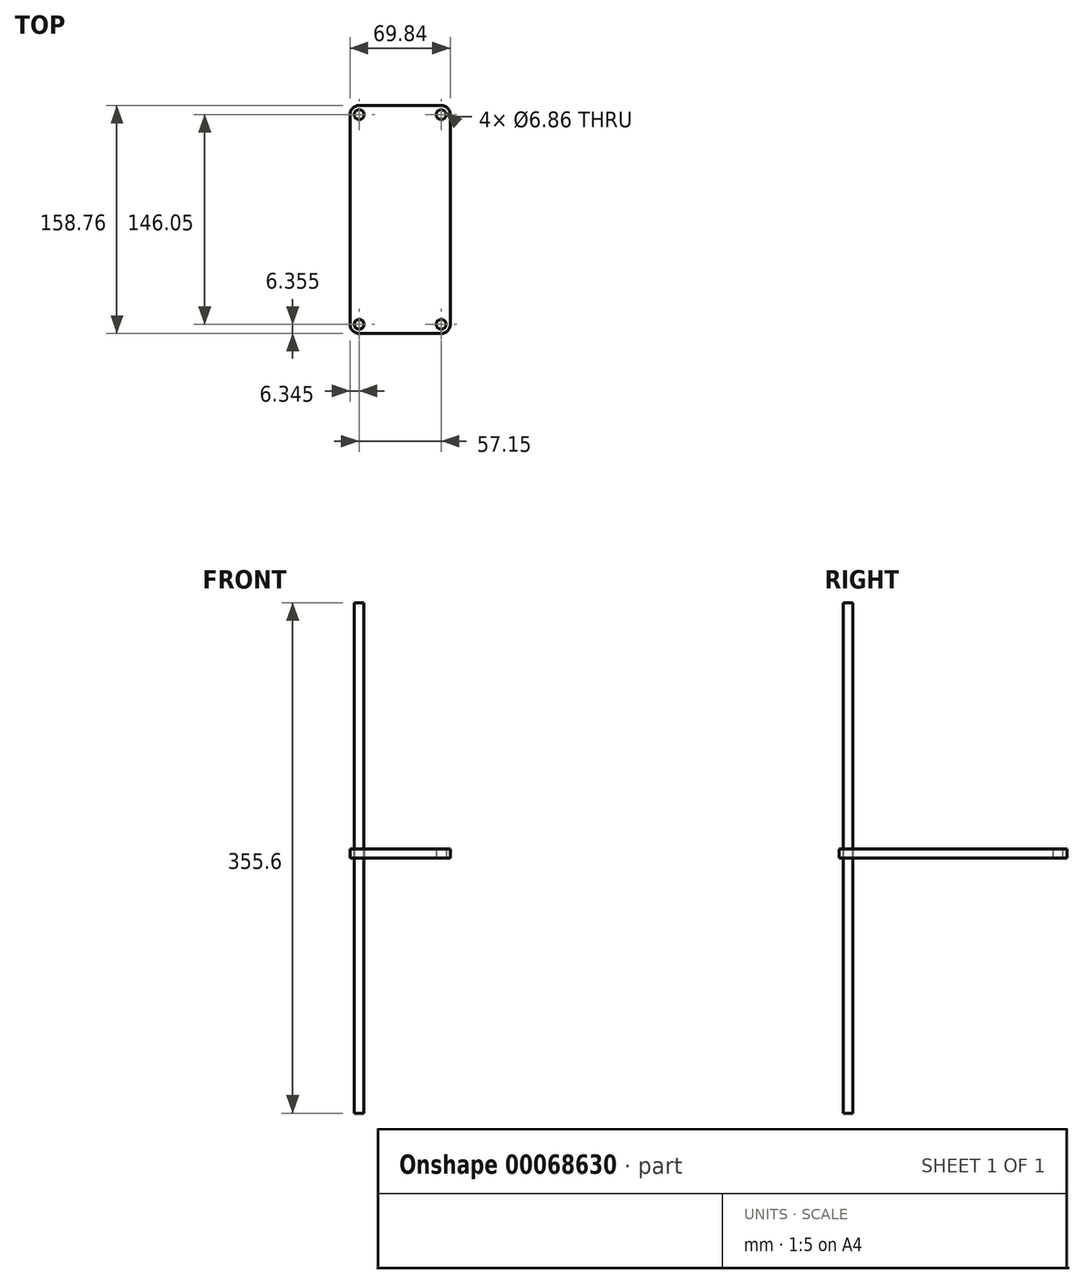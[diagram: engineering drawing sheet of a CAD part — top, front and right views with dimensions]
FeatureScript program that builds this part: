
annotation { "Feature Type Name" : "Feature", "Feature Type Description" : "" }
export const myFeature = defineFeature(function(context is Context, id is Id, definition is map)
    precondition{}
    {
        {
            var Q0;
            Q0=qCreatedBy(makeId("Top.planeOp"),FACE);
            var sketch = newSketch(context, id + "F0", { "sketchPlane" : qUnion([Q0])});
            skLineSegment(sketch, "E0", {"start": v(0, 79.38) * mm, "end": v(28.57, 79.38) * mm});
            skLineSegment(sketch, "E1", {"start": v(34.92, 73.03) * mm, "end": v(34.93, 0) * mm});
            skLineSegment(sketch, "E2.MirrorCS", {"start": v(0, 79.38) * mm, "end": v(-28.57, 79.38) * mm});
            skLineSegment(sketch, "E3.MirrorCS", {"start": v(-34.92, 73.03) * mm, "end": v(-34.93, 0) * mm});
            skLineSegment(sketch, "E4.MirrorCS", {"start": v(0, -79.38) * mm, "end": v(28.58, -79.38) * mm});
            skLineSegment(sketch, "E5.MirrorCS", {"start": v(34.93, -73.03) * mm, "end": v(34.93, 0) * mm});
            skLineSegment(sketch, "E6.MirrorCS", {"start": v(-34.93, -73.03) * mm, "end": v(-34.93, 0) * mm});
            skLineSegment(sketch, "E7.MirrorCS", {"start": v(0, -79.38) * mm, "end": v(-28.58, -79.38) * mm});
            skPoint(sketch, "E8.visualSharp", {"position": v(-34.92, 79.38) * mm});
            skArc(sketch, "E8.filletArc", {"start": v(-28.57, 79.38) * mm, "mid": v(-33.07, 77.52) * mm, "end": v(-34.93, 73.03) * mm});
            skPoint(sketch, "E9.visualSharp", {"position": v(-34.93, -79.38) * mm});
            skArc(sketch, "E9.filletArc", {"start": v(-34.93, -73.03) * mm, "mid": v(-33.07, -77.52) * mm, "end": v(-28.58, -79.37) * mm});
            skPoint(sketch, "E10.visualSharp", {"position": v(34.93, -79.38) * mm});
            skArc(sketch, "E10.filletArc", {"start": v(28.58, -79.38) * mm, "mid": v(33.07, -77.52) * mm, "end": v(34.93, -73.03) * mm});
            skPoint(sketch, "E11.visualSharp", {"position": v(34.92, 79.38) * mm});
            skArc(sketch, "E11.filletArc", {"start": v(34.92, 73.03) * mm, "mid": v(33.07, 77.52) * mm, "end": v(28.57, 79.37) * mm});
            skCircle(sketch, "E12", {"center": v(-28.57, 73.02) * mm, "radius": 3.43 * mm});
            skCircle(sketch, "E13", {"center": v(-28.58, -73.02) * mm, "radius": 3.43 * mm});
            skCircle(sketch, "E14", {"center": v(28.57, 73.02) * mm, "radius": 3.43 * mm});
            skCircle(sketch, "E15", {"center": v(28.58, -73.02) * mm, "radius": 3.43 * mm});
            skSolve(sketch);
        }
        {
            var Q0;
            Q0=makeQuery(id+"F0.imprint","IMPRINT",FACE,{"disambiguationData":[TD([[makeQuery(id+"F0.imprint","IMPRINT",EDGE,{"derivedFrom":sQuery(id+"F0.wireOp",EDGE,"E0")}),-1.0]])]});
            extrude(context, id + "F1", {"entities" : qUnion([Q0]), "depth" : 6.35 * mm});
        }
        {
            var Q0;
            Q0=makeQuery(id+"F1.opExtrude","CAP_FACE",FACE,{"disambiguationData":[OSD([sQuery(id+"F0.wireOp",EDGE,"E0"),sQuery(id+"F0.wireOp",EDGE,"E1"),sQuery(id+"F0.wireOp",EDGE,"E2.MirrorCS"),sQuery(id+"F0.wireOp",EDGE,"E3.MirrorCS"),sQuery(id+"F0.wireOp",EDGE,"E4.MirrorCS"),sQuery(id+"F0.wireOp",EDGE,"E5.MirrorCS"),sQuery(id+"F0.wireOp",EDGE,"E6.MirrorCS"),sQuery(id+"F0.wireOp",EDGE,"E7.MirrorCS"),sQuery(id+"F0.wireOp",EDGE,"E8.filletArc"),sQuery(id+"F0.wireOp",EDGE,"E9.filletArc"),sQuery(id+"F0.wireOp",EDGE,"E10.filletArc"),sQuery(id+"F0.wireOp",EDGE,"E11.filletArc"),sQuery(id+"F0.wireOp",EDGE,"E12"),sQuery(id+"F0.wireOp",EDGE,"E13"),sQuery(id+"F0.wireOp",EDGE,"E14"),sQuery(id+"F0.wireOp",EDGE,"E15")])],"isStart":true});
            var sketch = newSketch(context, id + "F2", { "sketchPlane" : qUnion([Q0])});
            skCircle(sketch, "E16", {"center": v(-28.58, 73.02) * mm, "radius": 3.28 * mm});
            skSolve(sketch);
        }
        {
            var Q0;
            Q0=makeQuery(id+"F2.imprint","IMPRINT",FACE,{"disambiguationData":[TD([[makeQuery(id+"F2.imprint","IMPRINT",EDGE,{"derivedFrom":sQuery(id+"F2.wireOp",EDGE,"E16")}),1.0]])]});
            extrude(context, id + "F3", {"entities" : qUnion([Q0]), "endBound" : BoundingType.SYMMETRIC, "depth" : 355.6 * mm});
        }
    });
